annotation { "Feature Type Name" : "Feature", "Feature Type Description" : "" }
export const myFeature = defineFeature(function(context is Context, id is Id, definition is map)
    precondition{}
    {
        {
            var Q0;
            Q0=qCreatedBy(makeId("Top.planeOp"),FACE);
            var sketch = newSketch(context, id + "F0", { "sketchPlane" : qUnion([Q0])});
            skCircle(sketch, "E0", {"center": v(0, 0) * mm, "radius": 40 * mm});
            skSolve(sketch);
        }
        {
            var Q0;
            Q0=qSketchRegion(id+"F0",true);
            extrude(context, id + "F1", {"entities" : qUnion([Q0]), "depth" : 110 * mm, "offsetDistance" : 25 * mm});
        }
        {
            var Q0;
            Q0=makeQuery(id+"F1.opExtrude","CAP_FACE",FACE,{"disambiguationData":[OSD([sQuery(id+"F0.wireOp",EDGE,"E0")])],"isStart":false});
            var sketch = newSketch(context, id + "F2", { "sketchPlane" : qUnion([Q0])});
            skCircle(sketch, "E1", {"center": v(0, 0) * mm, "radius": 37 * mm});
            skSolve(sketch);
        }
        {
            var Q0;
            Q0=qSketchRegion(id+"F2",true);
            extrude(context, id + "F3", {"entities" : qUnion([Q0]), "operationType" : NewBodyOperationType.REMOVE, "oppositeDirection" : true, "depth" : 104 * mm, "offsetDistance" : 25 * mm});
        }
        {
            var Q0;
            Q0=qCreatedBy(makeId("Front.planeOp"),FACE);
            var sketch = newSketch(context, id + "F4", { "sketchPlane" : qUnion([Q0])});
            skLineSegment(sketch, "E2", {"start": v(-40, 0) * mm, "end": v(-40, 110) * mm, "construction": true});
            skLineSegment(sketch, "E3", {"start": v(40, 110) * mm, "end": v(40, 0) * mm, "construction": true});
            skArc(sketch, "E4", {"start": v(0, 27.15) * mm, "mid": v(-4.81, 28.34) * mm, "end": v(-5.99, 23.52) * mm});
            skArc(sketch, "E5", {"start": v(5.99, 23.52) * mm, "mid": v(4.81, 28.34) * mm, "end": v(0, 27.15) * mm});
            skLineSegment(sketch, "E6", {"start": v(0, 15.02) * mm, "end": v(0, 12.97) * mm});
            skLineSegment(sketch, "E7", {"start": v(1.74, 16.04) * mm, "end": v(6.1, 23.72) * mm});
            skLineSegment(sketch, "E8.MirrorCS", {"start": v(-1.74, 16.04) * mm, "end": v(-6.1, 23.72) * mm});
            skPoint(sketch, "E9.visualSharp", {"position": v(0, 12.97) * mm});
            skArc(sketch, "E9.filletArc", {"start": v(-1.74, 16.04) * mm, "mid": v(0, 15.02) * mm, "end": v(1.74, 16.04) * mm});
            skPoint(sketch, "E10.orphan", {"position": v(0, 25.35) * mm});
            skArc(sketch, "E11", {"start": v(-6.6, 47.11) * mm, "mid": v(-11.4, 45.93) * mm, "end": v(-10.2, 41.12) * mm});
            skArc(sketch, "E12", {"start": v(0.4, 46.69) * mm, "mid": v(-2.88, 50.4) * mm, "end": v(-6.6, 47.11) * mm});
            skLineSegment(sketch, "E13", {"start": v(-0.95, 36.38) * mm, "end": v(0, 34.56) * mm});
            skLineSegment(sketch, "E14", {"start": v(0.11, 38.08) * mm, "end": v(0.4, 46.69) * mm});
            skLineSegment(sketch, "E15.MirrorCS", {"start": v(-2.97, 36.47) * mm, "end": v(-10.2, 41.12) * mm});
            skPoint(sketch, "E16.visualSharp", {"position": v(0, 34.56) * mm});
            skArc(sketch, "E16.filletArc", {"start": v(-2.97, 36.47) * mm, "mid": v(-0.95, 36.38) * mm, "end": v(0.11, 38.08) * mm});
            skPoint(sketch, "E17.orphan", {"position": v(-5.75, 45.52) * mm});
            skLineSegment(sketch, "E18.0", {"start": v(-8.4, 44.12) * mm, "end": v(-3.1, 46.91) * mm, "construction": true});
            skLineSegment(sketch, "E18.1", {"start": v(-8.4, 44.12) * mm, "end": v(-8.4, 44.12) * mm});
            skText(sketch, "E19", { "text": "Elisa", "fontName": "OpenSans-Bold.ttf"});
            skArc(sketch, "E20", {"start": v(1.45, 67.95) * mm, "mid": v(-2.4, 71.06) * mm, "end": v(-5.5, 67.19) * mm});
            skArc(sketch, "E21", {"start": v(5.35, 62.13) * mm, "mid": v(6.32, 67) * mm, "end": v(1.45, 67.95) * mm});
            skLineSegment(sketch, "E22", {"start": v(-3.67, 56.96) * mm, "end": v(-4.54, 55.1) * mm});
            skLineSegment(sketch, "E23", {"start": v(-1.67, 57.14) * mm, "end": v(5.53, 62.26) * mm});
            skLineSegment(sketch, "E24.MirrorCS", {"start": v(-4.82, 58.6) * mm, "end": v(-5.52, 67.41) * mm});
            skPoint(sketch, "E25.visualSharp", {"position": v(-4.54, 55.1) * mm});
            skArc(sketch, "E25.filletArc", {"start": v(-4.82, 58.6) * mm, "mid": v(-3.67, 56.96) * mm, "end": v(-1.67, 57.14) * mm});
            skPoint(sketch, "E26.orphan", {"position": v(0.7, 66.31) * mm});
            skLineSegment(sketch, "E27.0", {"start": v(-2.03, 67.58) * mm, "end": v(3.41, 65.04) * mm, "construction": true});
            skLineSegment(sketch, "E27.1", {"start": v(-2.03, 67.58) * mm, "end": v(-2.03, 67.58) * mm});
            const initialGuessF4  = {"E19": [-0.03, 0.0809, 1, 0, 0.0191]};
            skSetInitialGuess(sketch, initialGuessF4);
            skSolve(sketch);
        }
        {
            var Q0;
            Q0 = qSketchRegion(id + "F4", true);
            extrude(context, id + "F5", {"entities" : qUnion([Q0]), "operationType" : NewBodyOperationType.REMOVE, "endBound" : BoundingType.SYMMETRIC, "depth" : 90 * mm, "offsetDistance" : 25 * mm});
        }
        {
            var Q0;
            Q0=makeQuery(id+"F4.imprint","IMPRINT",FACE,{"disambiguationData":[TD([[makeQuery(id+"F4.imprint","IMPRINT",EDGE,{"derivedFrom":sQuery(id+"F4.wireOp",EDGE,"E19.sketch_text.stroke-0")}),-1.0]])]});
            var Q1;
            Q1=makeQuery(id+"F4.imprint","IMPRINT",FACE,{"disambiguationData":[TD([[makeQuery(id+"F4.imprint","IMPRINT",EDGE,{"derivedFrom":sQuery(id+"F4.wireOp",EDGE,"E19.sketch_text.stroke-12")}),-1.0]])]});
            var Q2;
            Q2=makeQuery(id+"F4.imprint","IMPRINT",FACE,{"disambiguationData":[TD([[makeQuery(id+"F4.imprint","IMPRINT",EDGE,{"derivedFrom":sQuery(id+"F4.wireOp",EDGE,"E19.sketch_text.stroke-16")}),-1.0]])]});
            var Q3;
            Q3=makeQuery(id+"F4.imprint","IMPRINT",FACE,{"disambiguationData":[TD([[makeQuery(id+"F4.imprint","IMPRINT",EDGE,{"derivedFrom":sQuery(id+"F4.wireOp",EDGE,"E19.sketch_text.stroke-21")}),-1.0]])]});
            var Q4;
            Q4=makeQuery(id+"F4.imprint","IMPRINT",FACE,{"disambiguationData":[TD([[makeQuery(id+"F4.imprint","IMPRINT",EDGE,{"derivedFrom":sQuery(id+"F4.wireOp",EDGE,"E19.sketch_text.stroke-25")}),-1.0]])]});
            var Q5;
            {var subQ0=sQuery(id+"F4.wireOp",EDGE,"E8.MirrorCS");var subQ1=sQuery(id+"F4.wireOp",EDGE,"E4");var subQ2=makeQuery(id+"F4.imprint","INTERSECT",VERTEX,{"disambiguationData":[OD(0.0)],"derivedFrom":[subQ1,subQ0]});Q5=makeQuery(id+"F4.imprint","IMPRINT",FACE,{"disambiguationData":[TD([[makeQuery(id+"F4.imprint","IMPRINT",EDGE,{"disambiguationData":[TD([[subQ2,1.0]])],"derivedFrom":subQ1}),1.0]])]});}
            var Q6;
            {var subQ0=sQuery(id+"F4.wireOp",EDGE,"E7");var subQ1=sQuery(id+"F4.wireOp",EDGE,"E5");var subQ2=makeQuery(id+"F4.imprint","INTERSECT",VERTEX,{"disambiguationData":[OD(0.0)],"derivedFrom":[subQ1,subQ0]});Q6=makeQuery(id+"F4.imprint","IMPRINT",FACE,{"disambiguationData":[TD([[makeQuery(id+"F4.imprint","IMPRINT",EDGE,{"disambiguationData":[TD([[subQ2,-1.0]])],"derivedFrom":subQ1}),1.0]])]});}
            var Q7;
            {var subQ0=sQuery(id+"F4.wireOp",EDGE,"E15.MirrorCS");var subQ1=sQuery(id+"F4.wireOp",EDGE,"E11");var subQ2=makeQuery(id+"F4.imprint","INTERSECT",VERTEX,{"disambiguationData":[OD(0.0)],"derivedFrom":[subQ1,subQ0]});Q7=makeQuery(id+"F4.imprint","IMPRINT",FACE,{"disambiguationData":[TD([[makeQuery(id+"F4.imprint","IMPRINT",EDGE,{"disambiguationData":[TD([[subQ2,1.0]])],"derivedFrom":subQ1}),1.0]])]});}
            var Q8;
            {var subQ0=sQuery(id+"F4.wireOp",EDGE,"E14");var subQ1=sQuery(id+"F4.wireOp",EDGE,"E12");var subQ2=makeQuery(id+"F4.imprint","INTERSECT",VERTEX,{"disambiguationData":[OD(0.0)],"derivedFrom":[subQ1,subQ0]});Q8=makeQuery(id+"F4.imprint","IMPRINT",FACE,{"disambiguationData":[TD([[makeQuery(id+"F4.imprint","IMPRINT",EDGE,{"disambiguationData":[TD([[subQ2,-1.0]])],"derivedFrom":subQ1}),1.0]])]});}
            var Q9;
            Q9=makeQuery(id+"F4.imprint","IMPRINT",FACE,{"disambiguationData":[TD([[makeQuery(id+"F4.imprint","IMPRINT",EDGE,{"derivedFrom":sQuery(id+"F4.wireOp",EDGE,"E19.sketch_text.stroke-51")}),-1.0]])]});
            extrude(context, id + "F6", {"entities" : qUnion([Q0, Q1, Q2, Q3, Q4, Q5, Q6, Q7, Q8, Q9]), "operationType" : NewBodyOperationType.REMOVE, "endBound" : BoundingType.SYMMETRIC, "depth" : 90 * mm, "offsetDistance" : 25 * mm});
        }
    });